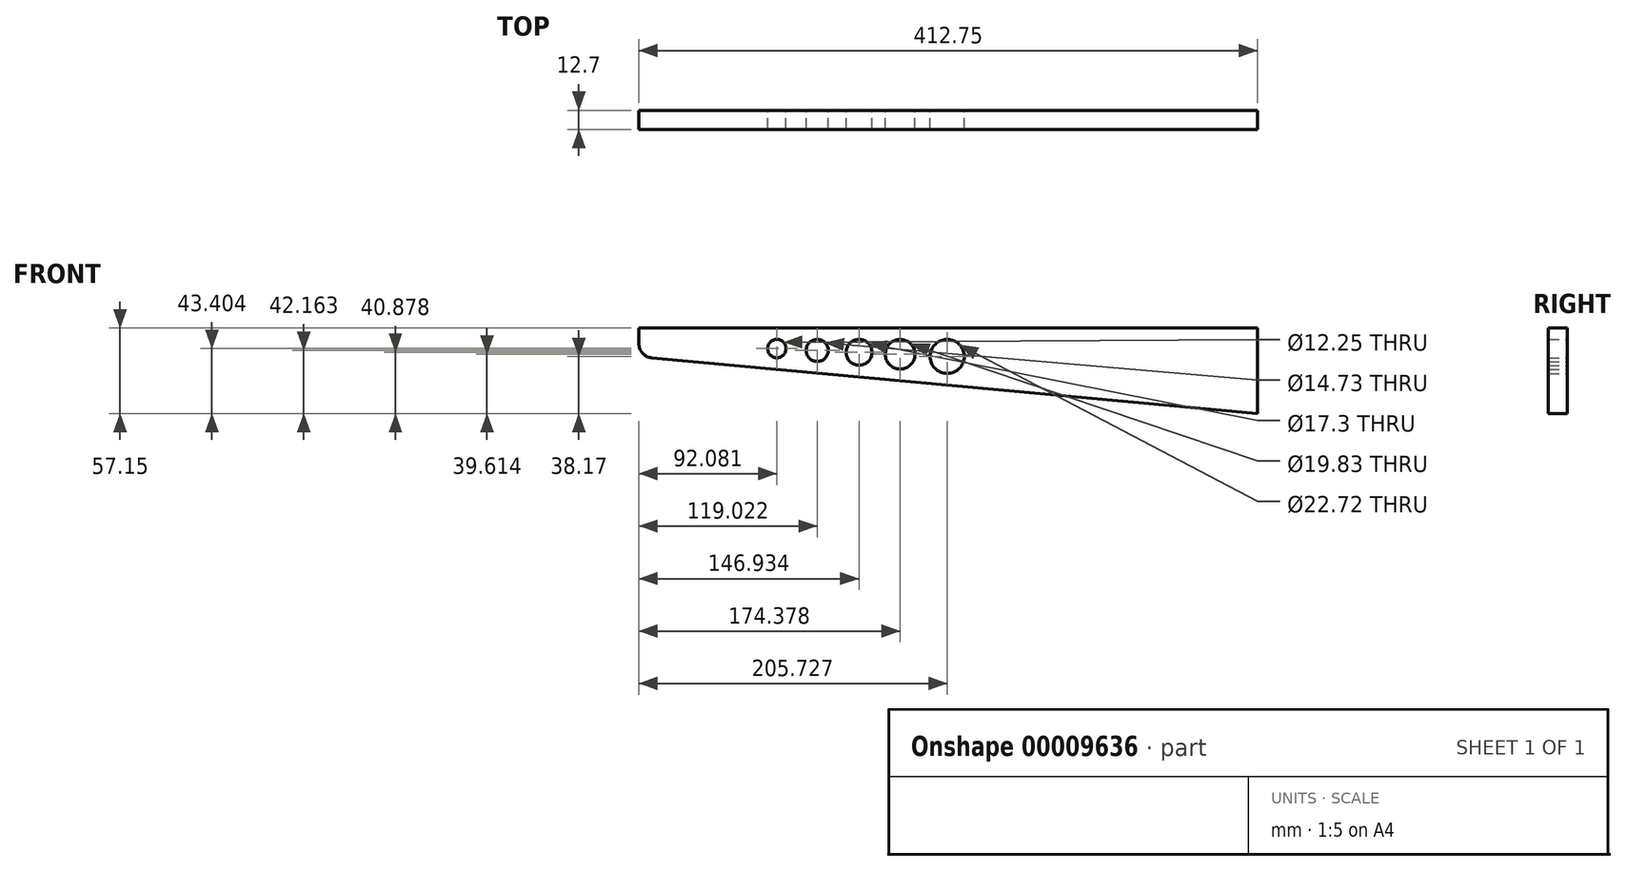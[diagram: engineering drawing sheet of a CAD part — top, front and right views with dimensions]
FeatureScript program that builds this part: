
annotation { "Feature Type Name" : "Feature", "Feature Type Description" : "" }
export const myFeature = defineFeature(function(context is Context, id is Id, definition is map)
    precondition{}
    {
        {
            var Q0;
            Q0=qCreatedBy(makeId("Front.planeOp"),FACE);
            var sketch = newSketch(context, id + "F0", { "sketchPlane" : qUnion([Q0])});
            skLineSegment(sketch, "E0", {"start": v(0, 0) * mm, "end": v(-412.75, 0) * mm});
            skLineSegment(sketch, "E1", {"start": v(-412.75, 0) * mm, "end": v(-412.75, -10.36) * mm});
            skLineSegment(sketch, "E2", {"start": v(-404.1, -19.85) * mm, "end": v(0, -57.15) * mm});
            skLineSegment(sketch, "E3", {"start": v(0, -57.15) * mm, "end": v(0, 0) * mm});
            skPoint(sketch, "E4.visualSharp", {"position": v(-412.75, -19.05) * mm});
            skArc(sketch, "E4.filletArc", {"start": v(-412.75, -10.36) * mm, "mid": v(-410.26, -16.78) * mm, "end": v(-404.1, -19.85) * mm});
            skLineSegment(sketch, "E5", {"start": v(10.5, -7.62) * mm, "end": v(-453.67, -7.62) * mm, "construction": true});
            skLineSegment(sketch, "E6", {"start": v(34.08, -52.64) * mm, "end": v(-453.67, -7.62) * mm, "construction": true});
            skCircle(sketch, "E7", {"center": v(-320.67, -13.75) * mm, "radius": 6.13 * mm});
            skCircle(sketch, "E8", {"center": v(-293.73, -14.99) * mm, "radius": 7.37 * mm});
            skCircle(sketch, "E9", {"center": v(-265.82, -16.27) * mm, "radius": 8.65 * mm});
            skCircle(sketch, "E10", {"center": v(-238.37, -17.54) * mm, "radius": 9.92 * mm});
            skCircle(sketch, "E11", {"center": v(-207.02, -18.98) * mm, "radius": 11.36 * mm});
            skSolve(sketch);
        }
        {
            var Q0;
            Q0=qSketchRegion(id+"F0",true);
            extrude(context, id + "F1", {"entities" : qUnion([Q0]), "depth" : 12.7 * mm});
        }
    });
